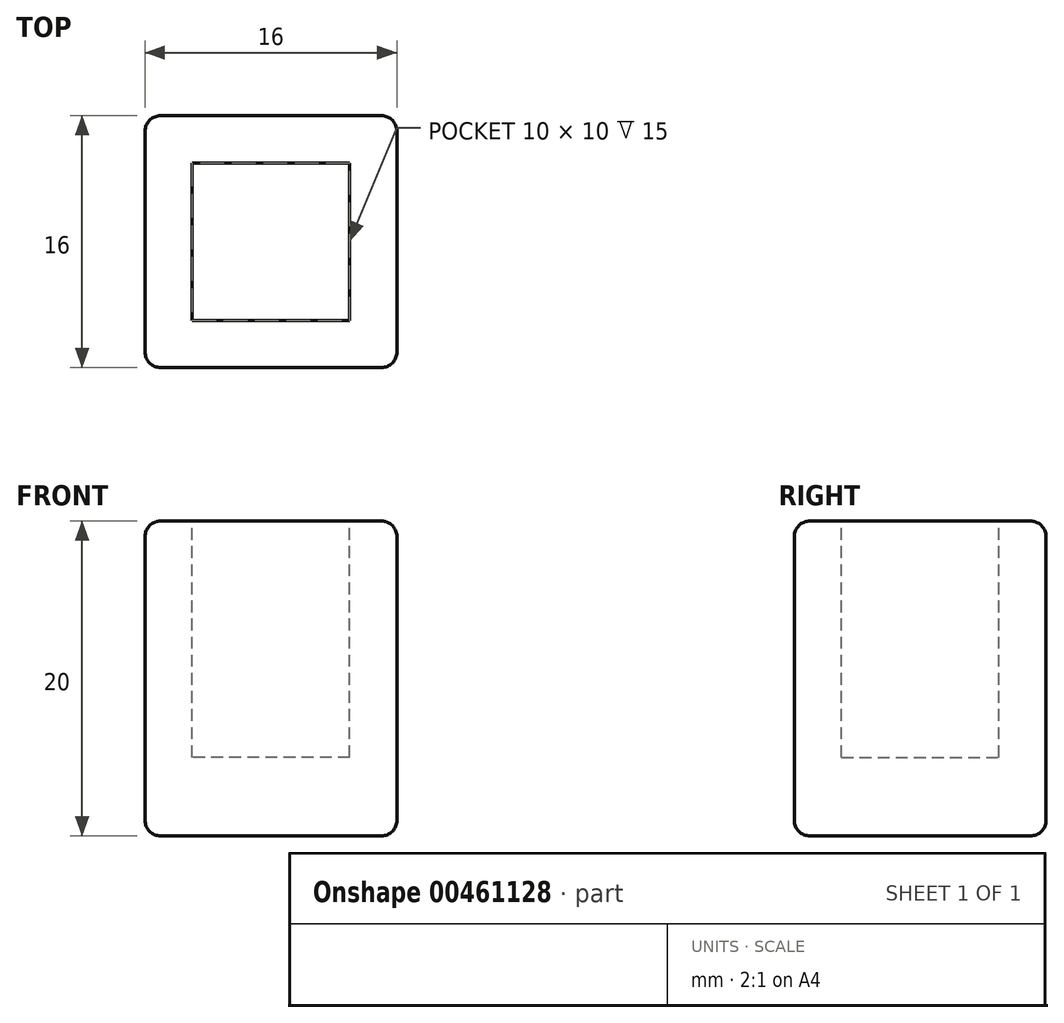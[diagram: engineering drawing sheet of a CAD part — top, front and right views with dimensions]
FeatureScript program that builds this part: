
annotation { "Feature Type Name" : "Feature", "Feature Type Description" : "" }
export const myFeature = defineFeature(function(context is Context, id is Id, definition is map)
    precondition{}
    {
        {
            var Q0;
            Q0=qCreatedBy(makeId("Top.planeOp"),FACE);
            var sketch = newSketch(context, id + "F0", { "sketchPlane" : qUnion([Q0])});
            skLineSegment(sketch, "E0.bottom", {"start": v(-61.23, 6.02) * mm, "end": v(-45.23, 6.02) * mm});
            skLineSegment(sketch, "E0.top", {"start": v(-61.23, -9.98) * mm, "end": v(-45.23, -9.98) * mm});
            skLineSegment(sketch, "E0.left", {"start": v(-61.23, 6.02) * mm, "end": v(-61.23, -9.98) * mm});
            skLineSegment(sketch, "E0.right", {"start": v(-45.23, 6.02) * mm, "end": v(-45.23, -9.98) * mm});
            skSolve(sketch);
        }
        {
            var Q0;
            Q0 = qSketchRegion(id + "F0", true);
            extrude(context, id + "F1", {"entities" : qUnion([Q0]), "depth" : 20 * mm});
        }
        {
            var Q0;
            Q0=makeQuery(id+"F1.opExtrude","CAP_FACE",FACE,{"disambiguationData":[OSD([sQuery(id+"F0.wireOp",EDGE,"E0.bottom"),sQuery(id+"F0.wireOp",EDGE,"E0.top"),sQuery(id+"F0.wireOp",EDGE,"E0.left"),sQuery(id+"F0.wireOp",EDGE,"E0.right")])],"isStart":false});
            var sketch = newSketch(context, id + "F2", { "sketchPlane" : qUnion([Q0])});
            skLineSegment(sketch, "E1.bottom", {"start": v(-61.23, 6.02) * mm, "end": v(-48.23, 6.02) * mm, "construction": true});
            skLineSegment(sketch, "E1.top", {"start": v(-61.23, -6.98) * mm, "end": v(-48.23, -6.98) * mm, "construction": true});
            skLineSegment(sketch, "E1.left", {"start": v(-61.23, 6.02) * mm, "end": v(-61.23, -6.98) * mm, "construction": true});
            skLineSegment(sketch, "E1.right", {"start": v(-48.23, 6.02) * mm, "end": v(-48.23, -6.98) * mm, "construction": true});
            skLineSegment(sketch, "E2.bottom", {"start": v(-48.23, -6.98) * mm, "end": v(-58.23, -6.98) * mm});
            skLineSegment(sketch, "E2.top", {"start": v(-48.23, 3.02) * mm, "end": v(-58.23, 3.02) * mm});
            skLineSegment(sketch, "E2.left", {"start": v(-48.23, -6.98) * mm, "end": v(-48.23, 3.02) * mm});
            skLineSegment(sketch, "E2.right", {"start": v(-58.23, -6.98) * mm, "end": v(-58.23, 3.02) * mm});
            skSolve(sketch);
        }
        {
            var Q0;
            Q0 = qSketchRegion(id + "F2", true);
            extrude(context, id + "F3", {"entities" : qUnion([Q0]), "operationType" : NewBodyOperationType.REMOVE, "oppositeDirection" : true, "depth" : 15 * mm});
        }
        {
            var Q0;
            Q0=makeQuery(id+"F1.opExtrude","SWEPT_FACE",FACE,{"disambiguationData":[OSD([sQuery(id+"F0.wireOp",EDGE,"E0.right")])]});
            var Q1;
            Q1=makeQuery(id+"F1.opExtrude","SWEPT_FACE",FACE,{"disambiguationData":[OSD([sQuery(id+"F0.wireOp",EDGE,"E0.top")])]});
            var Q2;
            Q2=makeQuery(id+"F1.opExtrude","SWEPT_FACE",FACE,{"disambiguationData":[OSD([sQuery(id+"F0.wireOp",EDGE,"E0.left")])]});
            var Q3;
            Q3=makeQuery(id+"F1.opExtrude","SWEPT_FACE",FACE,{"disambiguationData":[OSD([sQuery(id+"F0.wireOp",EDGE,"E0.bottom")])]});
            fillet(context, id + "F4", {"entities" : qUnion([Q0, Q1, Q2, Q3]), "radius" : 1 * mm, "tangentPropagation" : true, "allowEdgeOverflow" : false});
        }
    });
